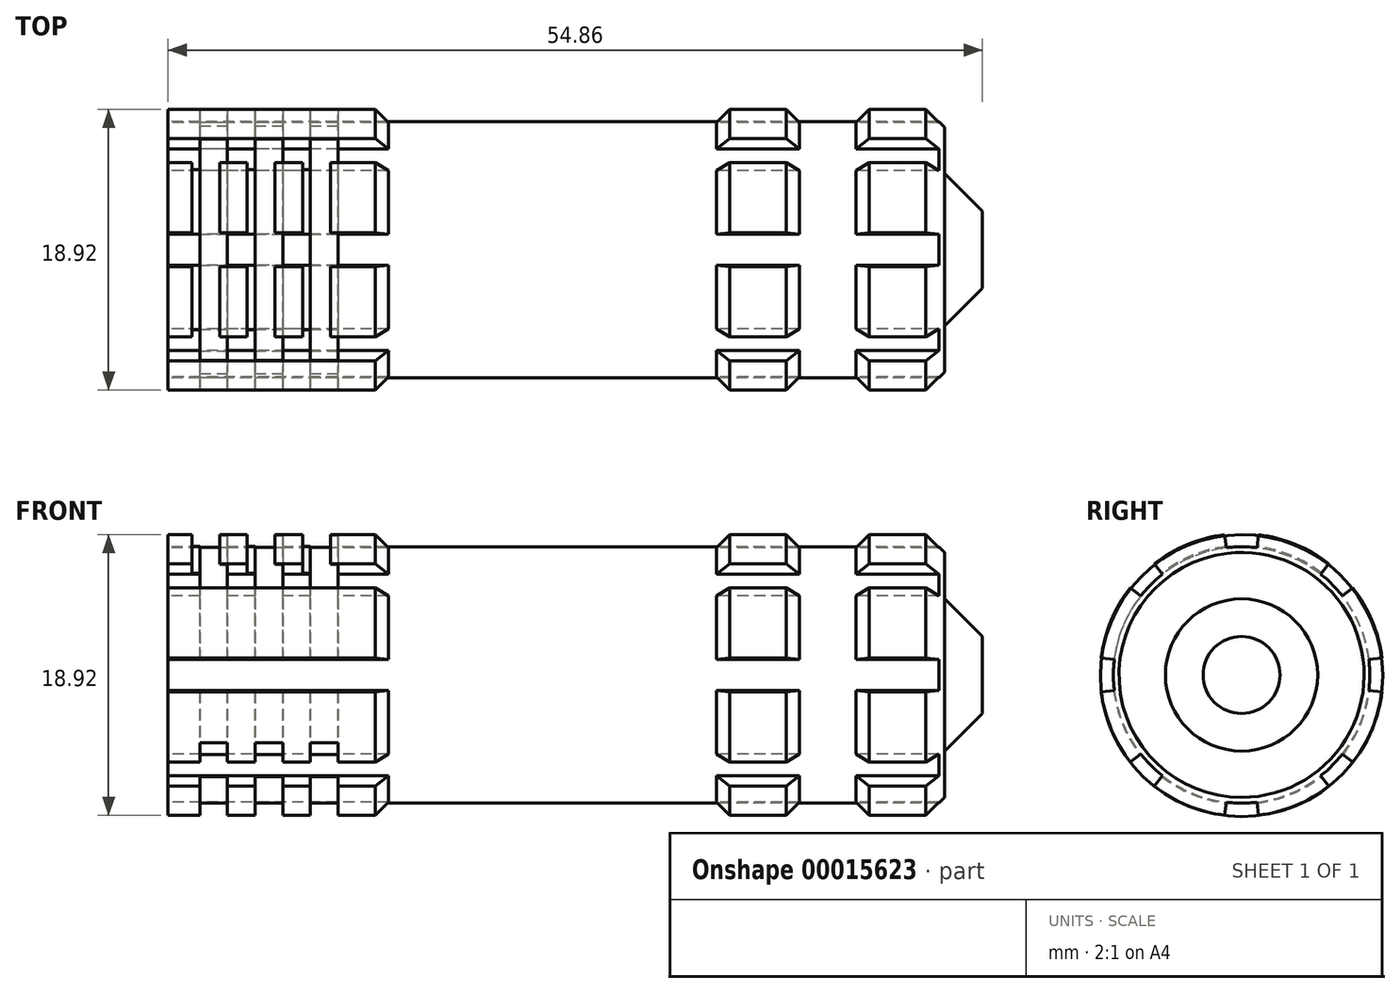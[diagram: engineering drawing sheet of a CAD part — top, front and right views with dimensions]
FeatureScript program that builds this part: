
annotation { "Feature Type Name" : "Feature", "Feature Type Description" : "" }
export const myFeature = defineFeature(function(context is Context, id is Id, definition is map)
    precondition{}
    {
        {
            var Q0;
            Q0=qCreatedBy(makeId("Front.planeOp"),FACE);
            var sketch = newSketch(context, id + "F0", { "sketchPlane" : qUnion([Q0])});
            skLineSegment(sketch, "E0", {"start": v(15.48, 9.52) * mm, "end": v(15.48, 8.64) * mm});
            skLineSegment(sketch, "E1", {"start": v(15.48, 8.64) * mm, "end": v(-2.04, 8.64) * mm});
            skLineSegment(sketch, "E2", {"start": v(-2.04, 8.64) * mm, "end": v(-2.04, 9.52) * mm});
            skLineSegment(sketch, "E3", {"start": v(-2.04, 9.52) * mm, "end": v(-21.1, 9.52) * mm});
            skLineSegment(sketch, "E4", {"start": v(-21.1, 9.52) * mm, "end": v(-21.1, 0) * mm});
            skLineSegment(sketch, "E5", {"start": v(21.83, 9.52) * mm, "end": v(21.83, 8.64) * mm});
            skLineSegment(sketch, "E6", {"start": v(21.83, 8.64) * mm, "end": v(24.88, 8.64) * mm});
            skLineSegment(sketch, "E7", {"start": v(24.88, 8.64) * mm, "end": v(24.88, 9.53) * mm});
            skLineSegment(sketch, "E8", {"start": v(15.48, 9.52) * mm, "end": v(21.83, 9.52) * mm});
            skLineSegment(sketch, "E9", {"start": v(24.88, 9.53) * mm, "end": v(31.23, 9.53) * mm});
            skLineSegment(sketch, "E10", {"start": v(31.23, 9.53) * mm, "end": v(31.23, 3.86) * mm});
            skLineSegment(sketch, "E11", {"start": v(31.23, 3.86) * mm, "end": v(33.77, 3.86) * mm});
            skLineSegment(sketch, "E12", {"start": v(33.77, 3.86) * mm, "end": v(33.77, 0) * mm});
            skLineSegment(sketch, "E13", {"start": v(-21.1, 0) * mm, "end": v(33.77, 0) * mm, "construction": true});
            skLineSegment(sketch, "E14", {"start": v(-21.1, 0) * mm, "end": v(33.77, 0) * mm});
            skSolve(sketch);
        }
        {
            var Q0;
            Q0 = qSketchRegion(id + "F0", true);
            var Q1;
            Q1=sQuery(id+"F0.wireOp",EDGE,"E4");
            var Q2;
            Q2=sQuery(id+"F0.wireOp",EDGE,"E3");
            var Q3;
            Q3=sQuery(id+"F0.wireOp",EDGE,"E2");
            var Q4;
            Q4=sQuery(id+"F0.wireOp",EDGE,"E1");
            var Q5;
            Q5=sQuery(id+"F0.wireOp",EDGE,"E0");
            var Q6;
            Q6=sQuery(id+"F0.wireOp",EDGE,"E8");
            var Q7;
            Q7=sQuery(id+"F0.wireOp",EDGE,"E5");
            var Q8;
            Q8=sQuery(id+"F0.wireOp",EDGE,"E6");
            var Q9;
            Q9=sQuery(id+"F0.wireOp",EDGE,"E7");
            var Q10;
            Q10=sQuery(id+"F0.wireOp",EDGE,"E9");
            var Q11;
            Q11=sQuery(id+"F0.wireOp",EDGE,"E10");
            var Q12;
            Q12=sQuery(id+"F0.wireOp",EDGE,"E11");
            var Q13;
            Q13=sQuery(id+"F0.wireOp",EDGE,"E12");
            var Q14;
            Q14=sQuery(id+"F0.wireOp",EDGE,"E13");
            revolve(context, id + "F1", {"entities" : qUnion([Q0]), "surfaceEntities" : qUnion([Q1, Q2, Q3, Q4, Q5, Q6, Q7, Q8, Q9, Q10, Q11, Q12, Q13]), "axis" : qUnion([Q14]), "revolveType" : RevolveType.FULL});
        }
        {
            var Q0;
            Q0=makeQuery(id+"F1.opRevolve","SWEPT_EDGE",EDGE,{"disambiguationData":[OSD([sQuery(id+"F0.wireOp",EDGE,"E2"),sQuery(id+"F0.wireOp",EDGE,"E3")])]});
            chamfer(context, id + "F2", {"entities" : qUnion([Q0]), "width" : 5.08 * mm, "tangentPropagation" : true});
        }
        {
            var Q0;
            Q0=makeQuery(id+"F1.opRevolve","SWEPT_FACE",FACE,{"disambiguationData":[OSD([sQuery(id+"F0.wireOp",EDGE,"E8")])]});
            var Q1;
            Q1=makeQuery(id+"F1.opRevolve","SWEPT_FACE",FACE,{"disambiguationData":[OSD([sQuery(id+"F0.wireOp",EDGE,"E9")])]});
            var Q2;
            Q2=makeQuery(id+"F1.opRevolve","SWEPT_FACE",FACE,{"disambiguationData":[OSD([sQuery(id+"F0.wireOp",EDGE,"E11")])]});
            chamfer(context, id + "F3", {"entities" : qUnion([Q0, Q1, Q2]), "width" : 1.27 * mm, "tangentPropagation" : true});
        }
        {
            var Q0;
            Q0=makeQuery(id+"F1.opRevolve","SWEPT_FACE",FACE,{"disambiguationData":[OSD([sQuery(id+"F0.wireOp",EDGE,"E4")])]});
            var sketch = newSketch(context, id + "F4", { "sketchPlane" : qUnion([Q0])});
            skLineSegment(sketch, "E15", {"start": v(0, 9.52) * mm, "end": v(0, -9.52) * mm, "construction": true});
            skLineSegment(sketch, "E16", {"start": v(-9.52, 0) * mm, "end": v(9.52, 0) * mm, "construction": true});
            skLineSegment(sketch, "E17", {"start": v(-6.74, -6.74) * mm, "end": v(6.74, 6.74) * mm, "construction": true});
            skLineSegment(sketch, "E18", {"start": v(-6.74, 6.74) * mm, "end": v(6.74, -6.74) * mm, "construction": true});
            skLineSegment(sketch, "E19", {"start": v(-5.88, 7.5) * mm, "end": v(0, 0) * mm});
            skLineSegment(sketch, "E20", {"start": v(0, 0) * mm, "end": v(-7.5, 5.88) * mm});
            skLineSegment(sketch, "E21", {"start": v(-5.88, 7.5) * mm, "end": v(-6.74, 6.74) * mm, "construction": true});
            skLineSegment(sketch, "E22", {"start": v(-7.5, 5.88) * mm, "end": v(-6.74, 6.74) * mm, "construction": true});
            skLineSegment(sketch, "E23", {"start": v(-1.14, 9.46) * mm, "end": v(0, 0) * mm});
            skLineSegment(sketch, "E24", {"start": v(0, 0) * mm, "end": v(1.14, 9.46) * mm});
            skLineSegment(sketch, "E25", {"start": v(1.14, 9.46) * mm, "end": v(0, 9.52) * mm, "construction": true});
            skLineSegment(sketch, "E26", {"start": v(-1.14, 9.46) * mm, "end": v(0, 9.52) * mm, "construction": true});
            skLineSegment(sketch, "E27", {"start": v(0, 0) * mm, "end": v(5.88, 7.5) * mm});
            skLineSegment(sketch, "E28", {"start": v(5.88, 7.5) * mm, "end": v(6.74, 6.74) * mm, "construction": true});
            skLineSegment(sketch, "E29", {"start": v(6.74, 6.74) * mm, "end": v(7.5, 5.88) * mm, "construction": true});
            skLineSegment(sketch, "E30", {"start": v(7.5, 5.88) * mm, "end": v(0, 0) * mm});
            skLineSegment(sketch, "E31", {"start": v(0, 0) * mm, "end": v(9.46, 1.14) * mm});
            skLineSegment(sketch, "E32", {"start": v(9.46, 1.14) * mm, "end": v(9.53, 0) * mm, "construction": true});
            skLineSegment(sketch, "E33", {"start": v(0, 0) * mm, "end": v(9.46, -1.14) * mm});
            skLineSegment(sketch, "E34", {"start": v(9.46, -1.14) * mm, "end": v(9.53, 0) * mm, "construction": true});
            skLineSegment(sketch, "E35", {"start": v(0, 0) * mm, "end": v(7.5, -5.88) * mm});
            skLineSegment(sketch, "E36", {"start": v(7.5, -5.88) * mm, "end": v(6.74, -6.74) * mm, "construction": true});
            skLineSegment(sketch, "E37", {"start": v(0, 0) * mm, "end": v(5.88, -7.5) * mm});
            skLineSegment(sketch, "E38", {"start": v(5.88, -7.5) * mm, "end": v(6.74, -6.74) * mm, "construction": true});
            skLineSegment(sketch, "E39", {"start": v(0, 0) * mm, "end": v(1.14, -9.46) * mm});
            skLineSegment(sketch, "E40", {"start": v(1.14, -9.46) * mm, "end": v(0, -9.52) * mm, "construction": true});
            skLineSegment(sketch, "E41", {"start": v(0, 0) * mm, "end": v(-1.14, -9.46) * mm});
            skLineSegment(sketch, "E42", {"start": v(-1.14, -9.46) * mm, "end": v(0, -9.52) * mm, "construction": true});
            skLineSegment(sketch, "E43", {"start": v(0, 0) * mm, "end": v(-5.88, -7.5) * mm});
            skLineSegment(sketch, "E44", {"start": v(-5.88, -7.5) * mm, "end": v(-6.74, -6.74) * mm, "construction": true});
            skLineSegment(sketch, "E45", {"start": v(0, 0) * mm, "end": v(-7.5, -5.88) * mm});
            skLineSegment(sketch, "E46", {"start": v(-7.5, -5.88) * mm, "end": v(-6.74, -6.74) * mm, "construction": true});
            skLineSegment(sketch, "E47", {"start": v(0, 0) * mm, "end": v(-9.46, -1.14) * mm});
            skLineSegment(sketch, "E48", {"start": v(-9.46, -1.14) * mm, "end": v(-9.52, 0) * mm, "construction": true});
            skLineSegment(sketch, "E49", {"start": v(0, 0) * mm, "end": v(-9.46, 1.14) * mm});
            skLineSegment(sketch, "E50", {"start": v(-9.46, 1.14) * mm, "end": v(-9.52, 0) * mm, "construction": true});
            skLineSegment(sketch, "E51", {"start": v(-5.88, 7.5) * mm, "end": v(-1.14, 9.46) * mm, "construction": true});
            skLineSegment(sketch, "E52", {"start": v(1.14, 9.46) * mm, "end": v(5.88, 7.5) * mm, "construction": true});
            skLineSegment(sketch, "E53", {"start": v(7.5, 5.88) * mm, "end": v(9.46, 1.14) * mm, "construction": true});
            skLineSegment(sketch, "E54", {"start": v(9.46, -1.14) * mm, "end": v(7.5, -5.88) * mm, "construction": true});
            skLineSegment(sketch, "E55", {"start": v(5.88, -7.5) * mm, "end": v(1.14, -9.46) * mm, "construction": true});
            skLineSegment(sketch, "E56", {"start": v(-1.14, -9.46) * mm, "end": v(-5.88, -7.5) * mm, "construction": true});
            skLineSegment(sketch, "E57", {"start": v(-7.5, -5.88) * mm, "end": v(-9.46, -1.14) * mm, "construction": true});
            skLineSegment(sketch, "E58", {"start": v(-9.46, 1.14) * mm, "end": v(-7.5, 5.88) * mm, "construction": true});
            skCircle(sketch, "E59", {"center": v(0, 0) * mm, "radius": 8.64 * mm});
            skLineSegment(sketch, "E60", {"start": v(0, 9.52) * mm, "end": v(0, 8.64) * mm, "construction": true});
            skSolve(sketch);
        }
        {
            var Q0;
            {var subQ3=sQuery(id+"F4.wireOp",EDGE,"E23");var subQ5=sQuery(id+"F4.wireOp",EDGE,"E59");var subQ7=makeQuery(id+"F4.imprint","INTERSECT",VERTEX,{"derivedFrom":[subQ3,subQ5]});Q0=makeQuery(id+"F4.imprint","IMPRINT",FACE,{"disambiguationData":[TD([[makeQuery(id+"F4.imprint","IMPRINT",EDGE,{"disambiguationData":[TD([[subQ7,1.0]])],"derivedFrom":subQ5}),-1.0]])]});}
            var Q1;
            {var subQ3=sQuery(id+"F4.wireOp",EDGE,"E27");var subQ5=sQuery(id+"F4.wireOp",EDGE,"E59");var subQ7=makeQuery(id+"F4.imprint","INTERSECT",VERTEX,{"derivedFrom":[subQ3,subQ5]});Q1=makeQuery(id+"F4.imprint","IMPRINT",FACE,{"disambiguationData":[TD([[makeQuery(id+"F4.imprint","IMPRINT",EDGE,{"disambiguationData":[TD([[subQ7,1.0]])],"derivedFrom":subQ5}),-1.0]])]});}
            var Q2;
            {var subQ3=sQuery(id+"F4.wireOp",EDGE,"E31");var subQ5=sQuery(id+"F4.wireOp",EDGE,"E59");var subQ7=makeQuery(id+"F4.imprint","INTERSECT",VERTEX,{"derivedFrom":[subQ3,subQ5]});Q2=makeQuery(id+"F4.imprint","IMPRINT",FACE,{"disambiguationData":[TD([[makeQuery(id+"F4.imprint","IMPRINT",EDGE,{"disambiguationData":[TD([[subQ7,1.0]])],"derivedFrom":subQ5}),-1.0]])]});}
            var Q3;
            {var subQ3=sQuery(id+"F4.wireOp",EDGE,"E35");var subQ5=sQuery(id+"F4.wireOp",EDGE,"E59");var subQ7=makeQuery(id+"F4.imprint","INTERSECT",VERTEX,{"derivedFrom":[subQ3,subQ5]});Q3=makeQuery(id+"F4.imprint","IMPRINT",FACE,{"disambiguationData":[TD([[makeQuery(id+"F4.imprint","IMPRINT",EDGE,{"disambiguationData":[TD([[subQ7,1.0]])],"derivedFrom":subQ5}),-1.0]])]});}
            var Q4;
            {var subQ3=sQuery(id+"F4.wireOp",EDGE,"E39");var subQ5=sQuery(id+"F4.wireOp",EDGE,"E59");var subQ7=makeQuery(id+"F4.imprint","INTERSECT",VERTEX,{"derivedFrom":[subQ3,subQ5]});Q4=makeQuery(id+"F4.imprint","IMPRINT",FACE,{"disambiguationData":[TD([[makeQuery(id+"F4.imprint","IMPRINT",EDGE,{"disambiguationData":[TD([[subQ7,1.0]])],"derivedFrom":subQ5}),-1.0]])]});}
            var Q5;
            {var subQ3=sQuery(id+"F4.wireOp",EDGE,"E43");var subQ5=sQuery(id+"F4.wireOp",EDGE,"E59");var subQ7=makeQuery(id+"F4.imprint","INTERSECT",VERTEX,{"derivedFrom":[subQ3,subQ5]});Q5=makeQuery(id+"F4.imprint","IMPRINT",FACE,{"disambiguationData":[TD([[makeQuery(id+"F4.imprint","IMPRINT",EDGE,{"disambiguationData":[TD([[subQ7,1.0]])],"derivedFrom":subQ5}),-1.0]])]});}
            var Q6;
            {var subQ3=sQuery(id+"F4.wireOp",EDGE,"E47");var subQ5=sQuery(id+"F4.wireOp",EDGE,"E59");var subQ7=makeQuery(id+"F4.imprint","INTERSECT",VERTEX,{"derivedFrom":[subQ3,subQ5]});Q6=makeQuery(id+"F4.imprint","IMPRINT",FACE,{"disambiguationData":[TD([[makeQuery(id+"F4.imprint","IMPRINT",EDGE,{"disambiguationData":[TD([[subQ7,1.0]])],"derivedFrom":subQ5}),-1.0]])]});}
            var Q7;
            {var subQ3=sQuery(id+"F4.wireOp",EDGE,"E19");var subQ5=sQuery(id+"F4.wireOp",EDGE,"E59");var subQ7=makeQuery(id+"F4.imprint","INTERSECT",VERTEX,{"derivedFrom":[subQ3,subQ5]});Q7=makeQuery(id+"F4.imprint","IMPRINT",FACE,{"disambiguationData":[TD([[makeQuery(id+"F4.imprint","IMPRINT",EDGE,{"disambiguationData":[TD([[subQ7,-1.0]])],"derivedFrom":subQ5}),-1.0]])]});}
            var Q8;
            Q8=makeQuery(id+"F1.opRevolve","SWEPT_FACE",FACE,{"disambiguationData":[OSD([sQuery(id+"F0.wireOp",EDGE,"E10")])]});
            extrude(context, id + "F5", {"entities" : qUnion([Q0, Q1, Q2, Q3, Q4, Q5, Q6, Q7]), "operationType" : NewBodyOperationType.REMOVE, "oppositeDirection" : true, "endBoundEntityFace" : qUnion([Q8]), "depth" : 76.2 * mm});
        }
        {
            var Q0;
            Q0=qCreatedBy(makeId("Front.planeOp"),FACE);
            var sketch = newSketch(context, id + "F6", { "sketchPlane" : qUnion([Q0])});
            skLineSegment(sketch, "E61", {"start": v(-21.13, 9.56) * mm, "end": v(-19.47, 9.56) * mm, "construction": true});
            skLineSegment(sketch, "E62", {"start": v(-19.47, 9.56) * mm, "end": v(-19.47, 8.72) * mm});
            skLineSegment(sketch, "E63", {"start": v(-19.47, 8.72) * mm, "end": v(-17.6, 8.72) * mm});
            skLineSegment(sketch, "E64", {"start": v(-17.6, 8.72) * mm, "end": v(-17.6, 9.56) * mm});
            skLineSegment(sketch, "E65", {"start": v(-17.6, 9.56) * mm, "end": v(-15.75, 9.56) * mm, "construction": true});
            skLineSegment(sketch, "E66", {"start": v(-15.75, 9.56) * mm, "end": v(-15.75, 8.72) * mm});
            skLineSegment(sketch, "E67", {"start": v(-15.75, 8.72) * mm, "end": v(-13.88, 8.72) * mm});
            skLineSegment(sketch, "E68", {"start": v(-13.88, 8.72) * mm, "end": v(-13.88, 9.56) * mm});
            skLineSegment(sketch, "E69", {"start": v(-13.88, 9.56) * mm, "end": v(-12.03, 9.56) * mm, "construction": true});
            skLineSegment(sketch, "E70", {"start": v(-12.03, 9.56) * mm, "end": v(-12.03, 8.72) * mm});
            skLineSegment(sketch, "E71", {"start": v(-12.03, 8.72) * mm, "end": v(-10.16, 8.72) * mm});
            skLineSegment(sketch, "E72", {"start": v(-10.16, 8.72) * mm, "end": v(-10.16, 9.56) * mm});
            skLineSegment(sketch, "E73", {"start": v(-10.16, 9.56) * mm, "end": v(-7.16, 9.56) * mm, "construction": true});
            skLineSegment(sketch, "E74", {"start": v(-21.13, 0) * mm, "end": v(-7.1, 0) * mm, "construction": true});
            skLineSegment(sketch, "E75", {"start": v(-21.13, 9.56) * mm, "end": v(-21.13, 0) * mm, "construction": true});
            skLineSegment(sketch, "E76", {"start": v(-19.47, 9.56) * mm, "end": v(-17.6, 9.56) * mm});
            skLineSegment(sketch, "E77", {"start": v(-15.75, 9.56) * mm, "end": v(-13.88, 9.56) * mm});
            skLineSegment(sketch, "E78", {"start": v(-12.03, 9.56) * mm, "end": v(-10.16, 9.56) * mm});
            skSolve(sketch);
        }
        {
            var Q0;
            Q0=qSketchRegion(id+"F6",true);
            var Q1;
            Q1=sQuery(id+"F6.wireOp",EDGE,"E74");
            revolve(context, id + "F7", {"operationType" : NewBodyOperationType.REMOVE, "entities" : qUnion([Q0]), "axis" : qUnion([Q1]), "revolveType" : RevolveType.SYMMETRIC, "oppositeDirection" : true, "angle" : 90 * degree});
        }
        {
            var Q0;
            Q0=qCreatedBy(makeId("Front.planeOp"),FACE);
            var sketch = newSketch(context, id + "F8", { "sketchPlane" : qUnion([Q0])});
            skLineSegment(sketch, "E79", {"start": v(-21.02, -8.7) * mm, "end": v(-18.96, -8.7) * mm, "construction": true});
            skLineSegment(sketch, "E80", {"start": v(-18.96, -8.7) * mm, "end": v(-18.96, -9.55) * mm});
            skLineSegment(sketch, "E81", {"start": v(-18.96, -9.55) * mm, "end": v(-17.08, -9.55) * mm});
            skLineSegment(sketch, "E82", {"start": v(-17.08, -9.55) * mm, "end": v(-17.08, -8.7) * mm});
            skLineSegment(sketch, "E83", {"start": v(-17.08, -8.7) * mm, "end": v(-15.24, -8.7) * mm, "construction": true});
            skLineSegment(sketch, "E84", {"start": v(-15.24, -8.7) * mm, "end": v(-15.24, -9.55) * mm});
            skLineSegment(sketch, "E85", {"start": v(-15.24, -9.55) * mm, "end": v(-13.36, -9.55) * mm});
            skLineSegment(sketch, "E86", {"start": v(-13.36, -9.55) * mm, "end": v(-13.36, -8.7) * mm});
            skLineSegment(sketch, "E87", {"start": v(-13.36, -8.7) * mm, "end": v(-11.52, -8.7) * mm, "construction": true});
            skLineSegment(sketch, "E88", {"start": v(-11.52, -8.7) * mm, "end": v(-11.52, -9.55) * mm});
            skLineSegment(sketch, "E89", {"start": v(-11.52, -9.55) * mm, "end": v(-9.65, -9.55) * mm});
            skLineSegment(sketch, "E90", {"start": v(-9.65, -9.55) * mm, "end": v(-9.65, -8.7) * mm});
            skLineSegment(sketch, "E91", {"start": v(-46.06, -8.7) * mm, "end": v(-9.65, -8.7) * mm, "construction": true});
            skLineSegment(sketch, "E92", {"start": v(-46.06, -0.05) * mm, "end": v(-21.02, -0.05) * mm, "construction": true});
            skLineSegment(sketch, "E93", {"start": v(-21.02, -0.05) * mm, "end": v(-21.02, -8.7) * mm, "construction": true});
            skLineSegment(sketch, "E94", {"start": v(-18.96, -8.7) * mm, "end": v(-17.08, -8.7) * mm});
            skLineSegment(sketch, "E95", {"start": v(-15.24, -8.7) * mm, "end": v(-13.36, -8.7) * mm});
            skLineSegment(sketch, "E96", {"start": v(-11.52, -8.7) * mm, "end": v(-9.65, -8.7) * mm});
            skLineSegment(sketch, "E97", {"start": v(-46.06, -0.05) * mm, "end": v(-46.06, -8.7) * mm, "construction": true});
            skSolve(sketch);
        }
        {
            var Q0;
            Q0=makeQuery(id+"F8.imprint","IMPRINT",FACE,{"disambiguationData":[TD([[makeQuery(id+"F8.imprint","IMPRINT",EDGE,{"derivedFrom":sQuery(id+"F8.wireOp",EDGE,"E88")}),1.0]])]});
            var Q1;
            Q1=makeQuery(id+"F8.imprint","IMPRINT",FACE,{"disambiguationData":[TD([[makeQuery(id+"F8.imprint","IMPRINT",EDGE,{"derivedFrom":sQuery(id+"F8.wireOp",EDGE,"E80")}),1.0]])]});
            var Q2;
            Q2=makeQuery(id+"F8.imprint","IMPRINT",FACE,{"disambiguationData":[TD([[makeQuery(id+"F8.imprint","IMPRINT",EDGE,{"derivedFrom":sQuery(id+"F8.wireOp",EDGE,"E84")}),1.0]])]});
            var Q3;
            Q3=sQuery(id+"F8.wireOp",EDGE,"E95");
            var Q4;
            Q4=sQuery(id+"F8.wireOp",EDGE,"E89");
            var Q5;
            Q5=sQuery(id+"F8.wireOp",EDGE,"E85");
            var Q6;
            Q6=sQuery(id+"F8.wireOp",EDGE,"E81");
            var Q7;
            Q7=sQuery(id+"F8.wireOp",EDGE,"E96");
            var Q8;
            Q8=sQuery(id+"F8.wireOp",EDGE,"E94");
            var Q9;
            Q9=sQuery(id+"F8.wireOp",EDGE,"E90");
            var Q10;
            Q10=sQuery(id+"F8.wireOp",EDGE,"E86");
            var Q11;
            Q11=sQuery(id+"F8.wireOp",EDGE,"E82");
            var Q12;
            Q12=sQuery(id+"F8.wireOp",EDGE,"E88");
            var Q13;
            Q13=sQuery(id+"F8.wireOp",EDGE,"E84");
            var Q14;
            Q14=sQuery(id+"F8.wireOp",EDGE,"E80");
            var Q15;
            Q15=sQuery(id+"F8.wireOp",EDGE,"E92");
            revolve(context, id + "F9", {"operationType" : NewBodyOperationType.REMOVE, "entities" : qUnion([Q0, Q1, Q2]), "surfaceEntities" : qUnion([Q3, Q4, Q5, Q6, Q7, Q8, Q9, Q10, Q11, Q12, Q13, Q14]), "axis" : qUnion([Q15]), "revolveType" : RevolveType.FULL, "oppositeDirection" : true});
        }
    });
